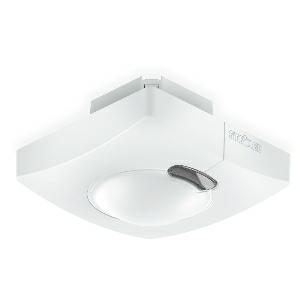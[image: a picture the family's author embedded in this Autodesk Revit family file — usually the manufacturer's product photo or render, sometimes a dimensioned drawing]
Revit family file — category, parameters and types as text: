
# Revit family: hf_3360_058227
name_source: partatom
category: Elektroinstallationen
revit_build: Autodesk Revit 2016 (Build: 20190508_0715(x64)
units: mm (PartAtom-declared; Revit-internal decimal feet)

## family parameters
Basisbauteil = Fläche
Beim Laden mit Abzugskörper schneiden = Nein
Bemaßung runder Anschluss = Durchmesser verwenden
Beschriftungsausrichtung beibehalten = Nein
Gemeinsam genutzt = Nein
Raumberechnungspunkt = Nein
Teiletyp = Normal

## types (1)
- HF 3360
    Apparent Load = 0 VA
    Beschreibung = Type: Motion detectors; Dimensions (L x W x H): 64 x 94 x 94 mm; Sensor Technology: High frequency; Application, place: Indoors; Application, room: function room / ancillary room, stairwell, WC / washroom, multi-storey / underground car park, Indoors; Installation site: wall, ceiling, corner; Installation: Concealed wiring; HF-system: 5,8 GHz; Mounting height: 2,00 – 4,00 m; Optimum mounting height: 2,8 m; Detection angle: 360 °; Sneak-by guard: Yes; Twilight setting TEACH: Yes; Time setting: 0 sec – 1092 min; Basic light level function: Yes; KNX functions: Photo-cell controller, Basic light level function, Light level, HVAC output, Constant-lighting control, Light output 2x, Presence output, Day / night function; With bus coupling: Yes; Settings via: ETS software, Remote control, Bus, Smart Remote; IP-rating: IP20; Material: Plastic; Colour: white; Colour, RAL: 9003; Version: KNX - concealed, sq.; PU1, EAN: 4007841058227
    Height = 94 mm  [stored 0.308399 ft]
    Hersteller = Steinel
    Length = 64 mm
    ModVariant = Nein
    Modell = 058227
    Mounting Type = Recessed
    Number of Poles = 1
    OnlyDefault = Ja
    Power Factor = 1
    Product Name = HF 3360
    Product group = Sensor-switched indoor light
    ProductGroupID = 30
    Protection Class = Protection class
    Protection Degree = IP 20
    RlxData = <blob elided: 26077 chars, md5=ae3975e9>
    SensorDataFile = {"IESDataFiles":[]}
    Typenbild = produkt1_058227.jpg
    Typenkommentare = Product without accessories
    URL = http://relux.com
    VarID = ---
    Voltage = 0 V
    Vorgabe-Ansicht = 1800 mm
    Weight = 0.00 kg
    Width = 94 mm  [stored 0.308399 ft]

note: [stored X ft] marks values corroborated as IEEE doubles in the binary element streams (Revit-internal decimal feet)

## geometry (parser evidence)
native form markers: Blend x4, Sweep x12
no freeform markers — native parametric forms only
